# Revit family: Shower_Kit-American_Standard-Traditional-1662607_Series
name_source: partatom
category: Plumbing Fixtures
revit_build: Autodesk Revit 2014 (Build: 20130308_1515(x64)
units: mm (PartAtom-declared; Revit-internal decimal feet)

## types (4) — shared parameters
Assembly Code = D2020300
CW Connection = Yes
CWFU = 3
Default Elevation = 68"
Description = Traditional Hand Shower Kit
HW Connection = Yes
HWFU = 3
Height = 30 1/8"
Installation Type = Wall Mounted
Length = 2 7/8"
Manufacturer = American Standard
Price = Prices may vary. Please consult Manufacturer Representative for most up-to-date price list.
URL = https://www.americanstandard-us.com
Vent Connection = No
WFU = 4
Warranty Information = Limited Lifetime Function and Finish Warranty
Waste Connection = No
Water Supply Connection Diameter = 1/2"
Width = 4 13/16"

## per-type parameters (varying)
| type | Finish | Material |
| 1662607.002 | Metal-American Standard-002-Polished Chrome | Metal-American Standard-002-Polished Chrome |
| 1662607.013 | Metal-American Standard-013-Polished Nickel | Metal-American Standard-013-Polished Nickel |
| 1662607.295 | Metal-American Standard-295-Brushed Nickel | Metal-American Standard-295-Brushed Nickel |
| 1662607.278 | Metal-American Standard-278-Legacy Bronze | Metal-American Standard-278-Legacy Bronze |

note: column(s) folded — value = type name in every type: Model

## geometry (parser evidence)
native form markers: Sweep x2
no freeform markers — native parametric forms only
